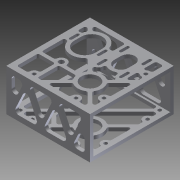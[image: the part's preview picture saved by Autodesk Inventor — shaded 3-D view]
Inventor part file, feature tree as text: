
AUTODESK INVENTOR PART (.ipt)
format: ipt  version: 2012 (Build 160160000, 160)  size: 867,840 bytes
history: native  units: in
note: dims shown in document units (in); Inventor stores cm internally (conversion verified against a paired STEP export)
features: extrude x7, sketch x5, fillet x3, projected_geometry x1
ambient origin geometry x8: Origin, YZ Plane, XZ Plane, XY Plane, X Axis, Y Axis, Z Axis, Center Point
bodies: Solid1 (feature_tree)
feature tree (16):
  extrude  "Extrusion1"  Depth=0.1875in
  sketch  "Sketch2"  dims[d4=0.25in d5=0.25in d6=6.0in d7=0.0in]
  extrude  "Extrusion2"  Depth=6.0in TaperAngle=0.0deg
  extrude  "Extrusion3"  Depth=1.25in
  extrude  "Extrusion4"  Depth=1.625in
  fillet  "Fillet2"  Radius=0.375in
  sketch  "Sketch6"  dims[d20=0.25in d21=0.125in d22=0.25in d24=0.25in d25=0.125in d27=0.125in d32=0.25in d33=0.0in d35=0.375in d36=0.375in d37=0.375in d38=0.375in d39=0.1719in d40=0.3438in d41=0.3438in d42=0.3438in d43=0.3438in d44=0.125in d46=0.125in d49=0.125in d50=0.125in d51=0.125in d52=0.125in d53=0.125in d54=0.125in d55=0.125in d56=0.125in d57=0.25in d58=0.0in d59=0.1719in d60=0.3438in d61=0.3438in d62=0.3438in d63=0.3438in d64=0.125in d65=0.125in d66=0.125in d67=0.125in d68=0.125in d69=0.125in d70=0.125in d71=0.125in d72=0.125in d73=0.125in d74=0.375in d76=0.375in d77=0.375in d78=0.375in d79=0.25in d80=0.0in d81=0.25in d88=0.125in d89=1.25in d90=1.5in d91=0.75in d92=0.5in d94=0.2in d96=0.9in d97=1.0in d98=0.5in d99=0.5in d101=2.0in d102=0.2in d103=0.8in d104=0.8in d105=0.7874in d107=1.6in d108=0.7874in d110=1.6in d114=1.0in d115=1.0in d116=1.625in d117=1.0in d119=0.2in d122=4.5in d123=1.3125in d124=0.366in d126=2.3in d127=0.25in d128=0.0in d129=0.375in d131=4.5in d132=0.125in d153=0.25in d154=0.125in d156=0.375in d157=0.375in d160=0.25in d161=0.125in d162=0.25in d163=0.125in d165=0.875in d166=0.125in d168=0.375in d169=0.25in d170=0.125in d171=1.0in d172=0.25in d177=0.125in d178=0.6in d179=0.25in d180=0.0in d181=0.125in d183=0.25in d185=0.25in d186=0.125in d188=1.5625in d190=1.3125in d191=0.366in d193=0.25in d194=0.125in d197=1.0in d198=1.176in d199=0.1in d200=0.0in d201=0.125in d203=0.25in d204=0.25in d205=0.125in d207=2.1875in d208=2.0312in d211=0.125in d212=0.3in d213=0.5in d214=0.25in d215=0.3125in d220=0.5in d221=1.5in d222=0.25in d224=0.1875in d225=2.3in d226=0.35in d227=0.25in d228=1.5in d229=1.5in d230=0.5821in d231=0.25in d232=1.5in d233=0.125in d234=0.25in d235=2.0in d236=0.25in d237=1.5in d238=0.3125in d239=0.7874in d241=3.0in d242=0.3937in d244=1.0in d246=1.5in d247=0.7874in d249=3.0in d250=0.3937in d252=1.0in d254=0.5in d255=0.25in d256=0.3125in d257=0.25in d258=0.5in d259=0.3125in d260=0.25in d262=0.75in d264=6.0in d267=0.25in d269=3.0in d270=6.0in d272=0.25in]
  fillet  "Fillet3"  Radius=0.875in
  extrude  "Extrusion5"  Depth=0.125in
  extrude  "Extrusion6"  Depth=0.25in
  fillet  "Fillet4"  Radius=0.25in
  extrude  "Extrusion7"  Depth=0.125in
  sketch  "Sketch1"  dims[d1=3.0in d2=0.1875in d3=0.25in]
  sketch  "Sketch4"  dims[d11=2.0312in d13=1.25in]
  sketch  "Sketch5"  dims[d15=2.625in d16=1.625in d18=0.375in d19=0.875in]
  projected_geometry  "Projected Loop1"
